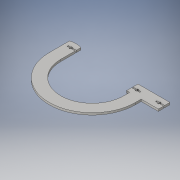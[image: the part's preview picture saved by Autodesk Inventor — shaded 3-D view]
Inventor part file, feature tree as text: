
AUTODESK INVENTOR PART (.ipt)
format: ipt  version: 2016 (Build 200138000, 138)  size: 164,352 bytes
history: native  units: in
note: dims shown in document units (in); Inventor stores cm internally (conversion verified against a paired STEP export)
features: extrude x1, sketch x1
ambient origin geometry x8: Origin, YZ Plane, XZ Plane, XY Plane, X Axis, Y Axis, Z Axis, Center Point
bodies: Body1 (feature_tree)
feature tree (2):
  extrude  "Extrusion2"  Depth=1.0in
  sketch  "Sketch1"  dims[d12=0.5in d16=1.0in d19=7.5in d20=0.625in d38=3.75in d48=2.776in d53=0.366in d54=0.063in d55=0.105in d56=0.229in d57=0.063in d58=0.366in d59=0.105in d60=0.229in d61=0.063in d62=0.2602in d63=0.5in d64=0.8818in d66=0.105in d67=0.4475in d68=0.4475in d69=0.4475in d70=0.4475in d71=1.5in d72=0.18in d73=0.0in]
